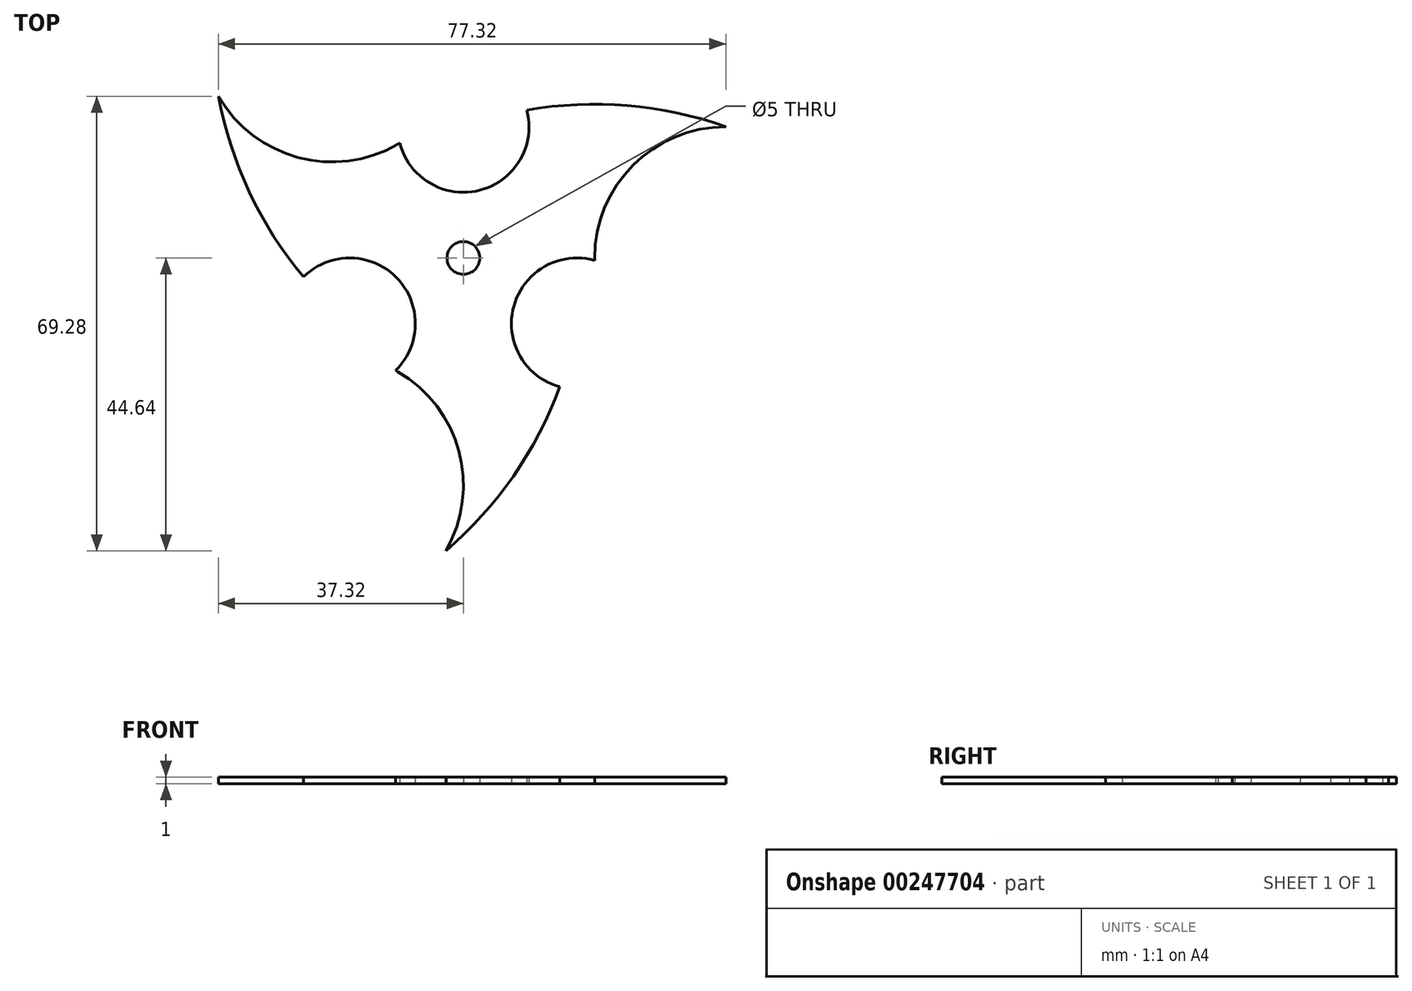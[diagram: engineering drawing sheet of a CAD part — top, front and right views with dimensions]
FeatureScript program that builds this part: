
annotation { "Feature Type Name" : "Feature", "Feature Type Description" : "" }
export const myFeature = defineFeature(function(context is Context, id is Id, definition is map)
    precondition{}
    {
        {
            var Q0;
            Q0=qCreatedBy(makeId("Top.planeOp"),FACE);
            var sketch = newSketch(context, id + "F0", { "sketchPlane" : qUnion([Q0])});
            skCircle(sketch, "E0", {"center": v(0, 0) * mm, "radius": 20 * mm});
            skLineSegment(sketch, "E1", {"start": v(0, 20) * mm, "end": v(40, 20) * mm});
            skLineSegment(sketch, "E2", {"start": v(17.32, -10) * mm, "end": v(-2.68, -44.64) * mm});
            skLineSegment(sketch, "E3", {"start": v(-17.32, -10) * mm, "end": v(-37.32, 24.64) * mm});
            skCircle(sketch, "E4.cCircle", {"center": v(0, 0) * mm, "radius": 20 * mm, "construction": true});
            skLineSegment(sketch, "E4.0", {"start": v(0, 20) * mm, "end": v(17.32, -10) * mm});
            skLineSegment(sketch, "E4.1", {"start": v(17.32, -10) * mm, "end": v(-17.32, -10) * mm});
            skLineSegment(sketch, "E4.2", {"start": v(-17.32, -10) * mm, "end": v(0, 20) * mm});
            skArc(sketch, "E5", {"start": v(-2.68, -44.64) * mm, "mid": v(10.3, -29.04) * mm, "end": v(17.32, -10) * mm});
            skArc(sketch, "E6", {"start": v(-37.32, 24.64) * mm, "mid": v(-30.3, 5.6) * mm, "end": v(-17.32, -10) * mm});
            skArc(sketch, "E7", {"start": v(40, 20) * mm, "mid": v(20, 23.43) * mm, "end": v(0, 20) * mm});
            skArc(sketch, "E8", {"start": v(-37.32, 24.64) * mm, "mid": v(-25.18, 15.32) * mm, "end": v(-10, 17.32) * mm});
            skArc(sketch, "E9", {"start": v(40, 20) * mm, "mid": v(25.86, 14.14) * mm, "end": v(20, 0) * mm});
            skArc(sketch, "E10", {"start": v(-2.68, -44.64) * mm, "mid": v(-0.68, -29.46) * mm, "end": v(-10, -17.32) * mm});
            skCircle(sketch, "E11", {"center": v(0, 0) * mm, "radius": 2.5 * mm});
            skCircle(sketch, "E12", {"center": v(0, 20) * mm, "radius": 10 * mm});
            skCircle(sketch, "E13", {"center": v(17.32, -10) * mm, "radius": 10 * mm});
            skCircle(sketch, "E14", {"center": v(-17.32, -10) * mm, "radius": 10 * mm});
            skSolve(sketch);
        }
        {
            var Q0;
            {var subQ0=sQuery(id+"F0.wireOp",EDGE,"E7");var subQ3=sQuery(id+"F0.wireOp",EDGE,"E12");var subQ5=makeQuery(id+"F0.imprint","INTERSECT",VERTEX,{"derivedFrom":[subQ0,subQ3]});Q0=makeQuery(id+"F0.imprint","IMPRINT",FACE,{"disambiguationData":[TD([[makeQuery(id+"F0.imprint","IMPRINT",EDGE,{"disambiguationData":[TD([[subQ5,1.0]])],"derivedFrom":subQ3}),-1.0]])]});}
            var Q1;
            {var subQ0=sQuery(id+"F0.wireOp",EDGE,"E5");var subQ3=sQuery(id+"F0.wireOp",EDGE,"E13");var subQ5=makeQuery(id+"F0.imprint","INTERSECT",VERTEX,{"derivedFrom":[subQ0,subQ3]});Q1=makeQuery(id+"F0.imprint","IMPRINT",FACE,{"disambiguationData":[TD([[makeQuery(id+"F0.imprint","IMPRINT",EDGE,{"disambiguationData":[TD([[subQ5,1.0]])],"derivedFrom":subQ3}),-1.0]])]});}
            var Q2;
            {var subQ0=sQuery(id+"F0.wireOp",EDGE,"E6");var subQ3=sQuery(id+"F0.wireOp",EDGE,"E14");var subQ5=makeQuery(id+"F0.imprint","INTERSECT",VERTEX,{"derivedFrom":[subQ0,subQ3]});Q2=makeQuery(id+"F0.imprint","IMPRINT",FACE,{"disambiguationData":[TD([[makeQuery(id+"F0.imprint","IMPRINT",EDGE,{"disambiguationData":[TD([[subQ5,1.0]])],"derivedFrom":subQ3}),-1.0]])]});}
            var Q3;
            {var subQ0=sQuery(id+"F0.wireOp",EDGE,"E9");Q3=makeQuery(id+"F0.imprint","IMPRINT",FACE,{"disambiguationData":[TD([[makeQuery(id+"F0.imprint","IMPRINT",EDGE,{"derivedFrom":subQ0}),-1.0]])]});}
            var Q4;
            {var subQ0=sQuery(id+"F0.wireOp",EDGE,"E8");Q4=makeQuery(id+"F0.imprint","IMPRINT",FACE,{"disambiguationData":[TD([[makeQuery(id+"F0.imprint","IMPRINT",EDGE,{"derivedFrom":subQ0}),-1.0]])]});}
            var Q5;
            {var subQ0=sQuery(id+"F0.wireOp",EDGE,"E10");Q5=makeQuery(id+"F0.imprint","IMPRINT",FACE,{"disambiguationData":[TD([[makeQuery(id+"F0.imprint","IMPRINT",EDGE,{"derivedFrom":subQ0}),-1.0]])]});}
            var Q6;
            {var subQ5=sQuery(id+"F0.wireOp",EDGE,"E0");var subQ7=makeQuery(id+"F0.imprint","INTERSECT",VERTEX,{"derivedFrom":[subQ5,sQuery(id+"F0.wireOp",EDGE,"E9")]});Q6=makeQuery(id+"F0.imprint","IMPRINT",FACE,{"disambiguationData":[TD([[makeQuery(id+"F0.imprint","IMPRINT",EDGE,{"disambiguationData":[TD([[subQ7,-1.0]])],"derivedFrom":subQ5}),1.0]])]});}
            var Q7;
            {var subQ5=sQuery(id+"F0.wireOp",EDGE,"E0");var subQ6=makeQuery(id+"F0.imprint","INTERSECT",VERTEX,{"derivedFrom":[subQ5,sQuery(id+"F0.wireOp",EDGE,"E8")]});Q7=makeQuery(id+"F0.imprint","IMPRINT",FACE,{"disambiguationData":[TD([[makeQuery(id+"F0.imprint","IMPRINT",EDGE,{"disambiguationData":[TD([[subQ6,1.0]])],"derivedFrom":subQ5}),1.0]])]});}
            var Q8;
            {var subQ1=sQuery(id+"F0.wireOp",EDGE,"E0");var subQ5=makeQuery(id+"F0.imprint","INTERSECT",VERTEX,{"derivedFrom":[subQ1,sQuery(id+"F0.wireOp",EDGE,"E10")]});Q8=makeQuery(id+"F0.imprint","IMPRINT",FACE,{"disambiguationData":[TD([[makeQuery(id+"F0.imprint","IMPRINT",EDGE,{"disambiguationData":[TD([[subQ5,1.0]])],"derivedFrom":subQ1}),1.0]])]});}
            var Q9;
            Q9=makeQuery(id+"F0.imprint","IMPRINT",FACE,{"disambiguationData":[TD([[makeQuery(id+"F0.imprint","IMPRINT",EDGE,{"derivedFrom":sQuery(id+"F0.wireOp",EDGE,"E11")}),-1.0]])]});
            extrude(context, id + "F1", {"entities" : qUnion([Q0, Q1, Q2, Q3, Q4, Q5, Q6, Q7, Q8, Q9]), "depth" : 1 * mm});
        }
    });
